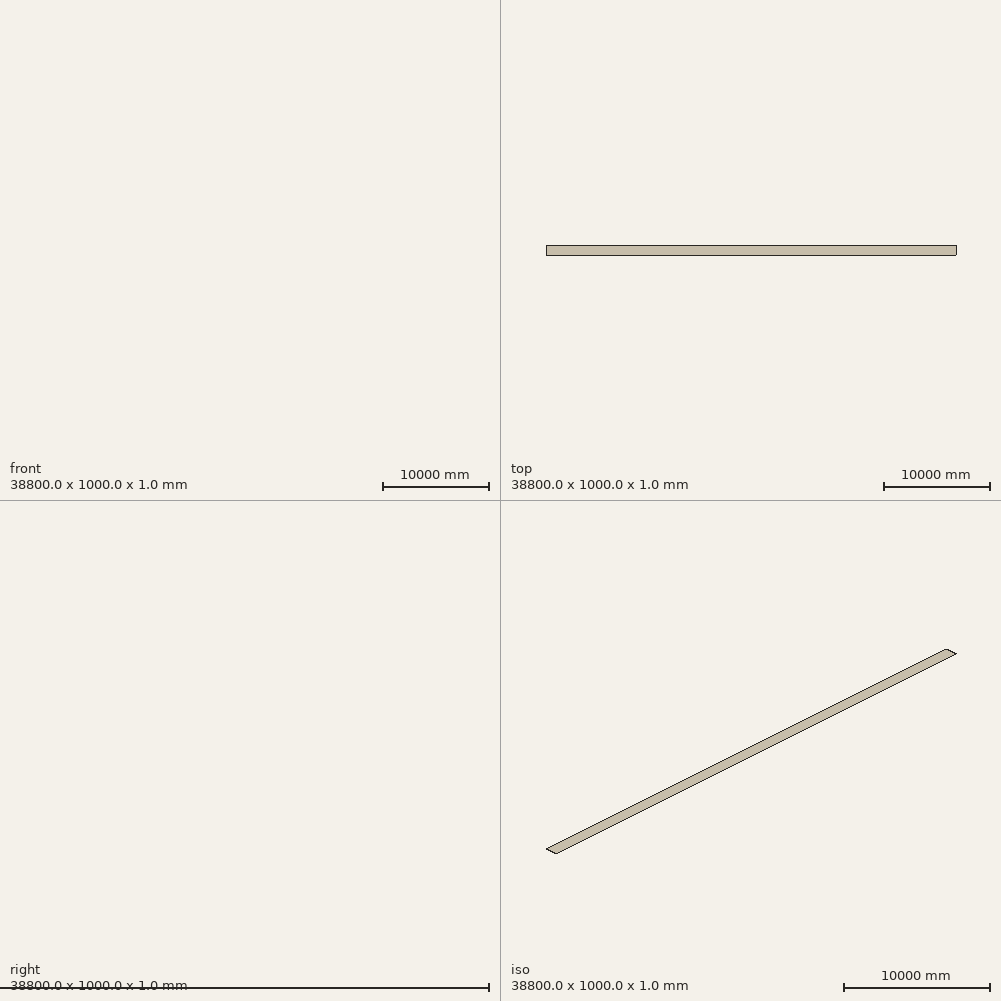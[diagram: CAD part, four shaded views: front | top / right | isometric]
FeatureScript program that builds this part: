
annotation { "Feature Type Name" : "Feature", "Feature Type Description" : "" }
export const myFeature = defineFeature(function(context is Context, id is Id, definition is map)
    precondition{}
    {
        {
            var Q0;
            Q0=qCreatedBy(makeId("Top.planeOp"),FACE);
            var sketch = newSketch(context, id + "F0", { "sketchPlane" : qUnion([Q0])});
            skLineSegment(sketch, "E0.bottom", {"start": v(0, 0) * mm, "end": v(-38800, 0) * mm});
            skLineSegment(sketch, "E0.top", {"start": v(0, -1000) * mm, "end": v(-38800, -1000) * mm});
            skLineSegment(sketch, "E0.left", {"start": v(0, 0) * mm, "end": v(0, -1000) * mm});
            skLineSegment(sketch, "E0.right", {"start": v(-38800, 0) * mm, "end": v(-38800, -1000) * mm});
            skSolve(sketch);
        }
        {
            var Q0;
            Q0=qSketchRegion(id+"F0",true);
            extrude(context, id + "F1", {"entities" : qUnion([Q0]), "depth" : 1 * mm});
        }
    });
